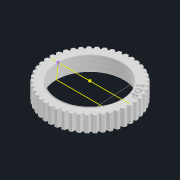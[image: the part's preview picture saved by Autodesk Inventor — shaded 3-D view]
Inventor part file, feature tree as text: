
AUTODESK INVENTOR PART (.ipt)
format: ipt  version: 2021.3 (Build 253353000, 353)  size: 597,504 bytes
history: native  units: mm
features: sketch x5, extrude x3, helix x2, draft x1, pattern_circular x1, projected_geometry x1
ambient origin geometry x8: Origin, YZ Plane, XZ Plane, XY Plane, X Axis, Y Axis, Z Axis, Center Point
bodies: Solid1 (feature_tree)
feature tree (13):
  extrude  "Extrusion1"  Depth=6.52mm TaperAngle=0.0deg
  draft  "FaceDraft1"
  sketch  "Sketch2"  dims[d7=2.0mm d8=9.0mm d9=10.0mm d10=1.047198mm d11=90.0deg d12=90.0deg d13=0.0mm d14=0.0mm d15=2.0mm d16=3.0mm d17=10.0mm d18=-1.047198mm d19=90.0deg d20=90.0deg d21=0.0mm d22=0.0mm d23=3.0mm d92=3.0mm]
  sketch  "Sketch4"  dims[d94=10.0mm d95=0.0mm d96=450.0mm d97=360.0deg]
  helix  "Coil1"  [1 undecoded]
  helix  "Coil2"  [1 undecoded]
  extrude  "Extrusion2"  Depth=450.0mm TaperAngle=360.0deg
  pattern_circular  "Circular Pattern3"  Angle=30.0deg  [1 undecoded]
  extrude  "Extrusion3"  Depth=1.0mm TaperAngle=0.0deg
  sketch  "Sketch1"  dims[d0=26.5mm d2=6.52mm d3=0.0mm d4=1.047198mm]
  sketch  "Sketch9"  dims[d99=1.2mm]
  sketch  "Sketch10"  dims[d100=30.0deg d101=30.0deg d102=1.0mm d103=0.0mm]
  projected_geometry  "Projected Loop1"
note: 3 required parameter values undecoded (feature->parameter linkage not recoverable at this tier; creation-order binding heuristic only, values carry confidence <= 0.55)
